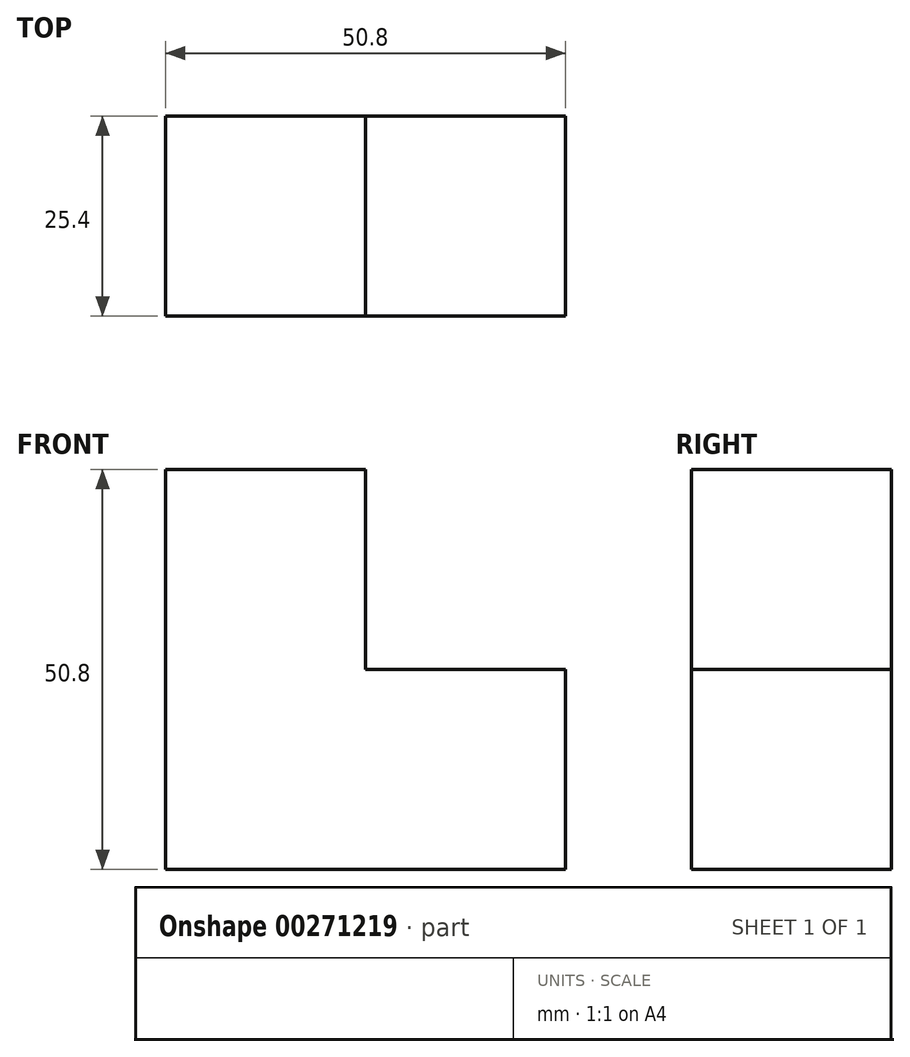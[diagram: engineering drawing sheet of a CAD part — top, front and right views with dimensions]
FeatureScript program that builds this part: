
annotation { "Feature Type Name" : "Feature", "Feature Type Description" : "" }
export const myFeature = defineFeature(function(context is Context, id is Id, definition is map)
    precondition{}
    {
        {
            var Q0;
            Q0=qCreatedBy(makeId("Front.planeOp"),FACE);
            var sketch = newSketch(context, id + "F0", { "sketchPlane" : qUnion([Q0])});
            skLineSegment(sketch, "E0", {"start": v(0, 0) * mm, "end": v(0, 50.8) * mm});
            skLineSegment(sketch, "E1", {"start": v(0, 0) * mm, "end": v(50.8, 0) * mm});
            skLineSegment(sketch, "E2", {"start": v(50.8, 0) * mm, "end": v(50.8, 25.4) * mm});
            skLineSegment(sketch, "E3", {"start": v(0, 50.8) * mm, "end": v(25.4, 50.8) * mm});
            skLineSegment(sketch, "E4", {"start": v(25.4, 50.8) * mm, "end": v(25.4, 25.4) * mm});
            skLineSegment(sketch, "E5", {"start": v(25.4, 25.4) * mm, "end": v(50.8, 25.4) * mm});
            skSolve(sketch);
        }
        {
            var Q0;
            Q0=makeQuery(id+"F0.imprint","IMPRINT",FACE,{"disambiguationData":[TD([[makeQuery(id+"F0.imprint","IMPRINT",EDGE,{"derivedFrom":sQuery(id+"F0.wireOp",EDGE,"E0")}),-1.0]])]});
            extrude(context, id + "F1", {"entities" : qUnion([Q0]), "depth" : 25.4 * mm});
        }
    });
